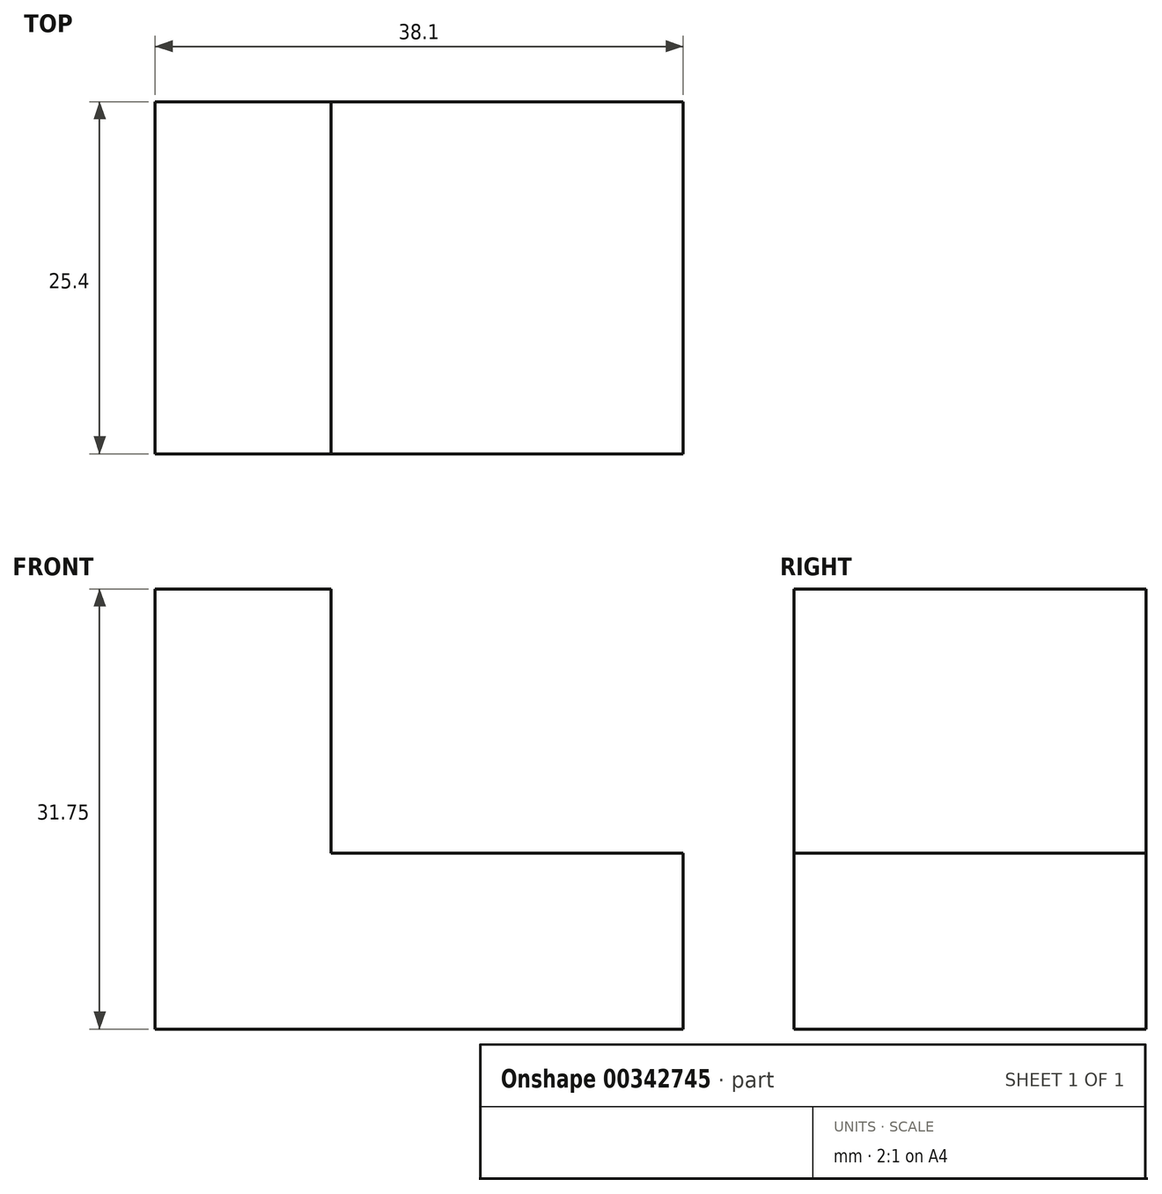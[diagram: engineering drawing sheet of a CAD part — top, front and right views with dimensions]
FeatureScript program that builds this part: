
annotation { "Feature Type Name" : "Feature", "Feature Type Description" : "" }
export const myFeature = defineFeature(function(context is Context, id is Id, definition is map)
    precondition{}
    {
        {
            var Q0;
            Q0=qCreatedBy(makeId("Front.planeOp"),FACE);
            var sketch = newSketch(context, id + "F0", { "sketchPlane" : qUnion([Q0])});
            skLineSegment(sketch, "E0", {"start": v(0, 0) * mm, "end": v(0, 31.75) * mm});
            skLineSegment(sketch, "E1", {"start": v(0, 31.75) * mm, "end": v(12.7, 31.75) * mm});
            skLineSegment(sketch, "E2", {"start": v(12.7, 31.75) * mm, "end": v(12.7, 12.7) * mm});
            skLineSegment(sketch, "E3", {"start": v(12.7, 12.7) * mm, "end": v(38.1, 12.7) * mm});
            skLineSegment(sketch, "E4", {"start": v(38.1, 12.7) * mm, "end": v(38.1, 0) * mm});
            skLineSegment(sketch, "E5", {"start": v(0, 0) * mm, "end": v(38.1, 0) * mm});
            skLineSegment(sketch, "E6", {"start": v(0, 31.75) * mm, "end": v(0, 0) * mm});
            skSolve(sketch);
        }
        {
            var Q0;
            Q0 = qSketchRegion(id + "F0", true);
            extrude(context, id + "F1", {"entities" : qUnion([Q0]), "oppositeDirection" : true, "depth" : 25.4 * mm});
        }
    });
